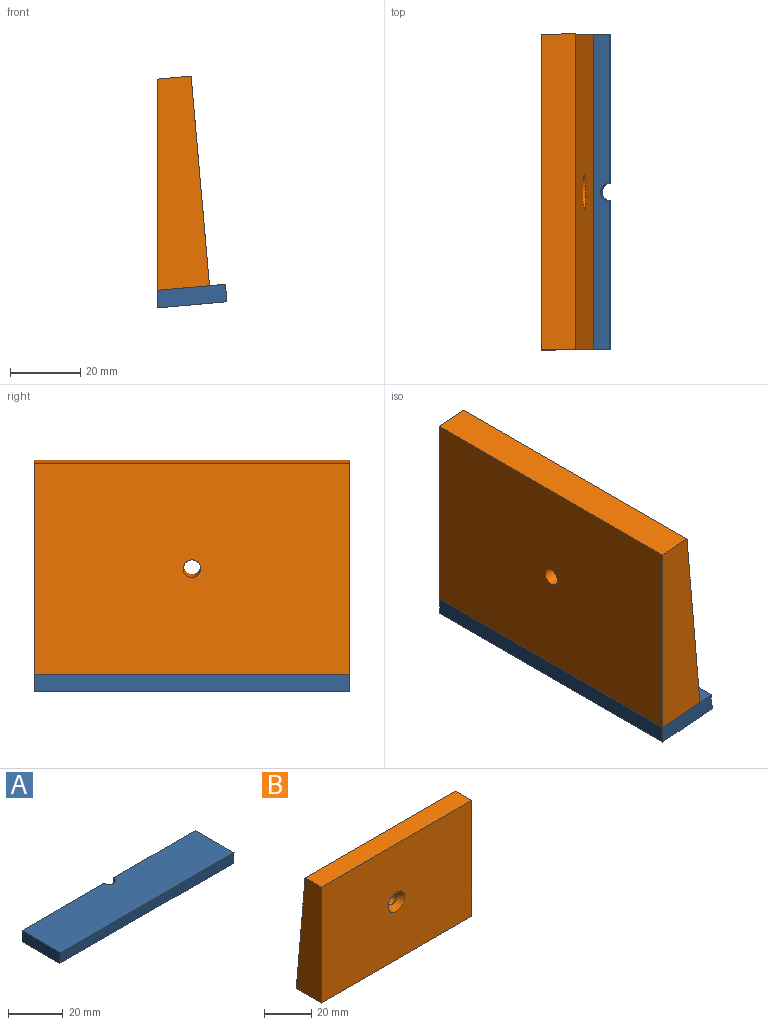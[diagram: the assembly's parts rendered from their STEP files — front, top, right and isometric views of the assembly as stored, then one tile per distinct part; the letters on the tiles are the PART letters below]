
ASSEMBLY  parts=2 mates=1
PART A: 8 faces, bbox 90x20x5 mm
  f0: plane 90x20mm, normal (0,0,1), area 1790.2mm2, adj f1,f2,f3,f4,f6,f7
  f1: plane 42.5x5mm, normal (0,1,0), area 212.5mm2, adj f0,f3,f5,f7
  f2: plane 42.5x5mm, normal (0,1,0), area 212.5mm2, adj f0,f4,f5,f7
  f3: plane 20x5mm, normal (1,0,0), area 98.9mm2, adj f0,f1,f5,f6
  f4: plane 20x5mm, normal (-1,0,0), area 98.9mm2, adj f0,f2,f5,f6
  f5: plane 90x19.56mm, normal (0,0,-1), area 1750.8mm2, adj f1,f2,f3,f4,f6,f7
  f6: plane 90x5mm, normal (0,-1,-0.09), area 451.7mm2, adj f0,f3,f4,f5
  f7: cylinder r=2.5mm len=5mm, axis (0,0,1), area 39.3mm2, adj f0,f1,f2,f5
PART B: 8 faces, bbox 90.1x15.1x60.1 mm
  f0: plane 60x15mm, normal (1,0,0), area 742.5mm2, adj f1,f3,f4,f5
  f1: plane 90x9.75mm, normal (0,0,1), area 877.6mm2, adj f0,f2,f4,f5
  f2: plane 60x15mm, normal (-1,0,0), area 742.5mm2, adj f1,f3,f4,f5
  f3: plane 90x15mm, normal (0,0,-1), area 1350mm2, adj f0,f2,f4,f5
  f4: plane 90.09x60.09mm, normal (0,1,0.09), area 5400.9mm2, adj f0,f1,f2,f3,f6
  f5: plane 90x60mm, normal (0,-1,0), area 5321.5mm2, adj f0,f1,f2,f3,f7
  f6: cylinder r=2.5mm len=10.09mm, axis (0,-1,0), area 155.1mm2, adj f4,f7
  f7: cone r=2.5mm half-angle=45deg, axis (0,-1,0), area 83.3mm2, adj f5,f6
PLACE A rot(axis=(0.71,0.71,0.03),176.5deg) t=(-0.22,0,-32.64)mm
PLACE B rot(axis=(-0.04,-0.04,1),90.1deg) t=(12.33,0,1.08)mm
MATE fastened B.f3 <-> A.f5  axis (0.09,0,-1) through (0,0,-30.11)mm
